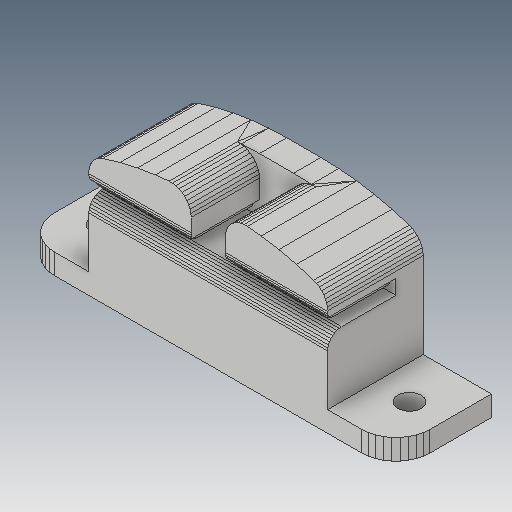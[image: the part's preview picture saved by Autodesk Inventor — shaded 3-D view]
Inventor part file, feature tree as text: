
AUTODESK INVENTOR PART (.ipt)
format: ipt  version: 2017 (Build 210142000, 142)  size: 488,448 bytes
history: native  units: mm
features: other x2, hole x1, sketch x1, projected_geometry x1
ambient origin geometry x8: Origin, YZ Plane, XZ Plane, XY Plane, X Axis, Y Axis, Z Axis, Center Point
bodies: Solid1 (feature_tree)
feature tree (5):
  other  "Y Belt Clamp"
  other  "MeshFeature1"
  hole  "Hole1"  [1 undecoded]
  sketch  "Sketch2"  dims[d0=3.4mm d1=6.0mm d2=4.0mm d3=2.0mm d4=90.0deg d5=8.0mm d6=20.594885mm]
  projected_geometry  "Projected Loop1"
note: 1 required parameter value undecoded (feature->parameter linkage not recoverable at this tier; creation-order binding heuristic only, values carry confidence <= 0.55)
